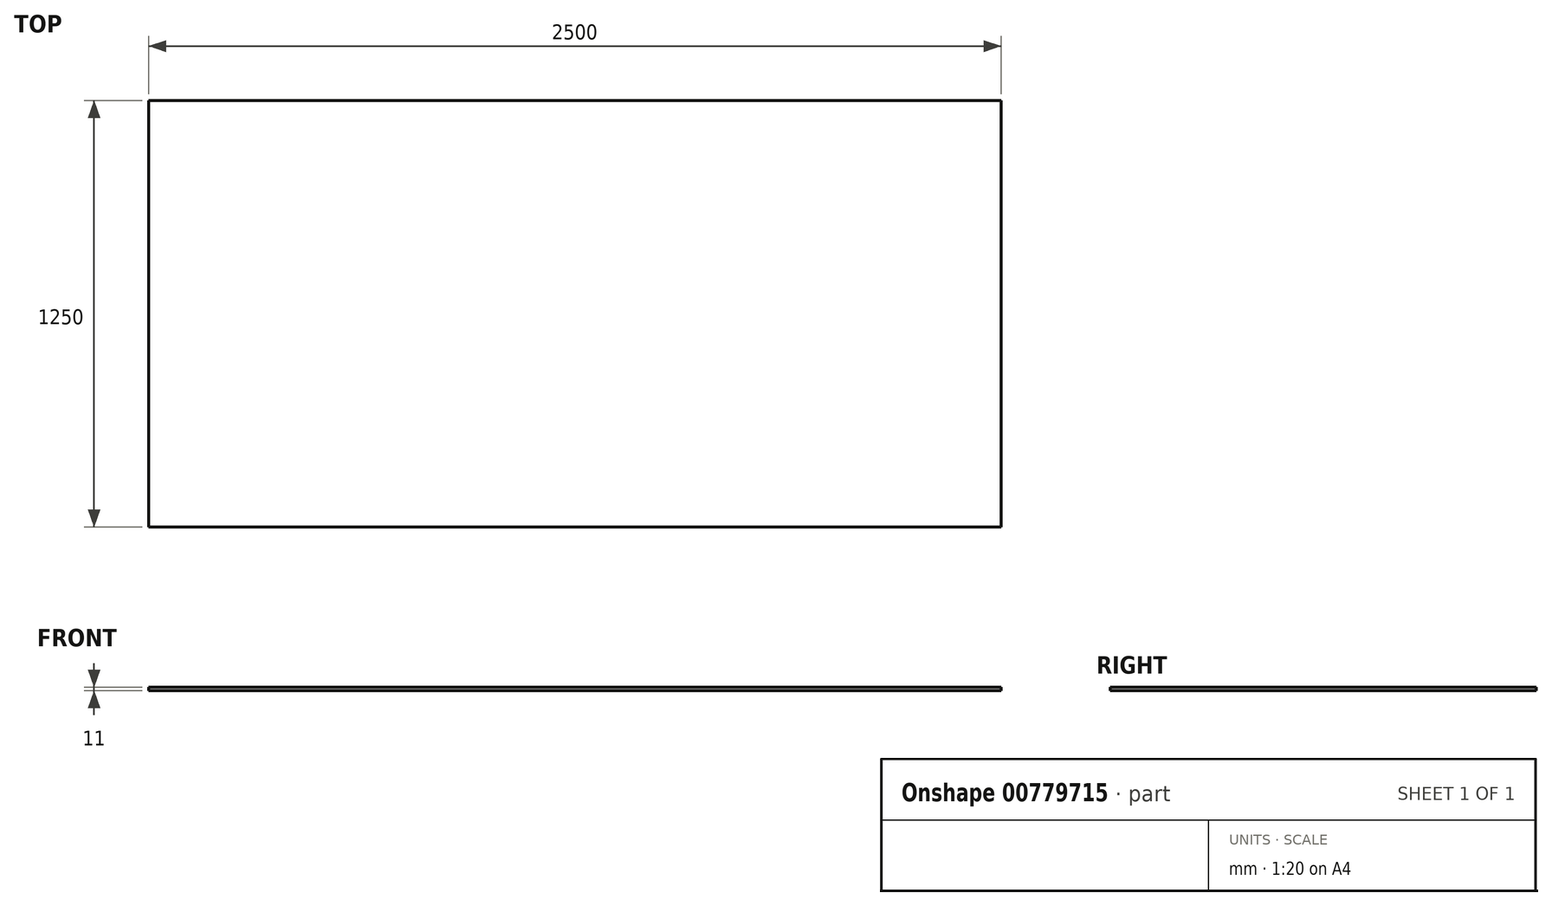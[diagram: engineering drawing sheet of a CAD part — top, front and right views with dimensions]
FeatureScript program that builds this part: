
annotation { "Feature Type Name" : "Feature", "Feature Type Description" : "" }
export const myFeature = defineFeature(function(context is Context, id is Id, definition is map)
    precondition{}
    {
        {
            var Q0;
            Q0=qCreatedBy(makeId("Top.planeOp"),FACE);
            var sketch = newSketch(context, id + "F0", { "sketchPlane" : qUnion([Q0])});
            skLineSegment(sketch, "E0.bottom", {"start": v(1250, -625) * mm, "end": v(-1250, -625) * mm});
            skLineSegment(sketch, "E0.top", {"start": v(1250, 625) * mm, "end": v(-1250, 625) * mm});
            skLineSegment(sketch, "E0.left", {"start": v(1250, -625) * mm, "end": v(1250, 625) * mm});
            skLineSegment(sketch, "E0.right", {"start": v(-1250, -625) * mm, "end": v(-1250, 625) * mm});
            skPoint(sketch, "E0.middle", {"position": v(0, 0) * mm});
            skLineSegment(sketch, "E1", {"start": v(-1250, 25) * mm, "end": v(1250, 25) * mm});
            skLineSegment(sketch, "E2", {"start": v(0, 625) * mm, "end": v(0, -625) * mm});
            skSolve(sketch);
        }
        {
            var Q0;
            Q0 = qSketchRegion(id + "F0", true);
            extrude(context, id + "F1", {"entities" : qUnion([Q0]), "depth" : 11 * mm, "offsetDistance" : 25 * mm});
        }
    });
